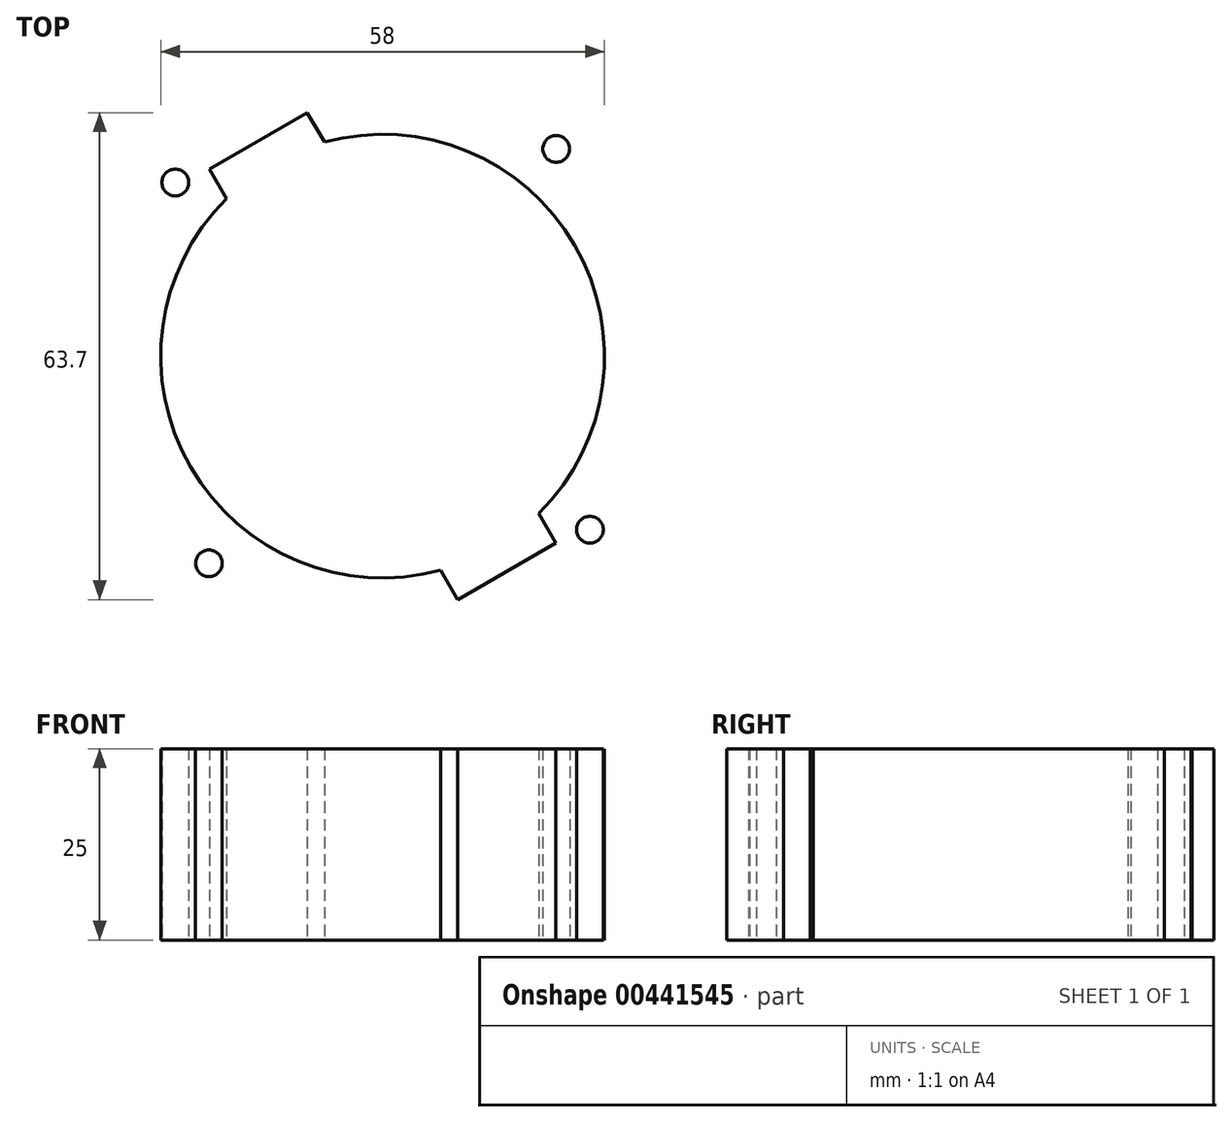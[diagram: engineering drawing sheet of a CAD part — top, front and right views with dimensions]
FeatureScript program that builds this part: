
annotation { "Feature Type Name" : "Feature", "Feature Type Description" : "" }
export const myFeature = defineFeature(function(context is Context, id is Id, definition is map)
    precondition{}
    {
        {
            var Q0;
            Q0=qCreatedBy(makeId("Top.planeOp"),FACE);
            var sketch = newSketch(context, id + "F0", { "sketchPlane" : qUnion([Q0])});
            skCircle(sketch, "E0", {"center": v(0, 0) * mm, "radius": 29 * mm});
            skLineSegment(sketch, "E1.bottom", {"start": v(-9.84, 31.85) * mm, "end": v(-22.66, 24.45) * mm});
            skLineSegment(sketch, "E1.top", {"start": v(22.66, -24.45) * mm, "end": v(9.84, -31.85) * mm});
            skLineSegment(sketch, "E1.left", {"start": v(-9.84, 31.85) * mm, "end": v(22.66, -24.45) * mm});
            skLineSegment(sketch, "E1.right", {"start": v(-22.66, 24.45) * mm, "end": v(9.84, -31.85) * mm});
            skCircle(sketch, "E2", {"center": v(22.7, 27.1) * mm, "radius": 1.75 * mm});
            skCircle(sketch, "E3", {"center": v(27.1, -22.7) * mm, "radius": 1.75 * mm});
            skCircle(sketch, "E4", {"center": v(-27.1, 22.7) * mm, "radius": 1.75 * mm});
            skCircle(sketch, "E5", {"center": v(-22.7, -27.1) * mm, "radius": 1.75 * mm});
            skSolve(sketch);
        }
        {
            var Q0;
            {var subQ0=sQuery(id+"F0.wireOp",EDGE,"E1.right");var subQ1=sQuery(id+"F0.wireOp",EDGE,"E0");var subQ2=makeQuery(id+"F0.imprint","INTERSECT",VERTEX,{"disambiguationData":[OD(0.0)],"derivedFrom":[subQ1,subQ0]});Q0=makeQuery(id+"F0.imprint","IMPRINT",FACE,{"disambiguationData":[TD([[makeQuery(id+"F0.imprint","IMPRINT",EDGE,{"disambiguationData":[TD([[subQ2,1.0]])],"derivedFrom":subQ1}),1.0]])]});}
            var Q1;
            {var subQ0=sQuery(id+"F0.wireOp",EDGE,"E1.left");var subQ1=sQuery(id+"F0.wireOp",EDGE,"E0");var subQ2=makeQuery(id+"F0.imprint","INTERSECT",VERTEX,{"disambiguationData":[OD(0.0)],"derivedFrom":[subQ1,subQ0]});Q1=makeQuery(id+"F0.imprint","IMPRINT",FACE,{"disambiguationData":[TD([[makeQuery(id+"F0.imprint","IMPRINT",EDGE,{"disambiguationData":[TD([[subQ2,1.0]])],"derivedFrom":subQ1}),1.0]])]});}
            var Q2;
            {var subQ5=sQuery(id+"F0.wireOp",EDGE,"E1.top");Q2=makeQuery(id+"F0.imprint","IMPRINT",FACE,{"disambiguationData":[TD([[makeQuery(id+"F0.imprint","IMPRINT",EDGE,{"derivedFrom":subQ5}),-1.0]])]});}
            var Q3;
            {var subQ5=sQuery(id+"F0.wireOp",EDGE,"E1.bottom");Q3=makeQuery(id+"F0.imprint","IMPRINT",FACE,{"disambiguationData":[TD([[makeQuery(id+"F0.imprint","IMPRINT",EDGE,{"derivedFrom":subQ5}),1.0]])]});}
            var Q4;
            {var subQ0=sQuery(id+"F0.wireOp",EDGE,"E1.right");var subQ1=sQuery(id+"F0.wireOp",EDGE,"E0");var subQ2=makeQuery(id+"F0.imprint","INTERSECT",VERTEX,{"disambiguationData":[OD(0.0)],"derivedFrom":[subQ1,subQ0]});Q4=makeQuery(id+"F0.imprint","IMPRINT",FACE,{"disambiguationData":[TD([[makeQuery(id+"F0.imprint","IMPRINT",EDGE,{"disambiguationData":[TD([[subQ2,-1.0]])],"derivedFrom":subQ1}),1.0]])]});}
            var Q5;
            Q5=makeQuery(id+"F0.imprint","IMPRINT",FACE,{"disambiguationData":[TD([[makeQuery(id+"F0.imprint","IMPRINT",EDGE,{"derivedFrom":sQuery(id+"F0.wireOp",EDGE,"E3")}),1.0]])]});
            var Q6;
            Q6=makeQuery(id+"F0.imprint","IMPRINT",FACE,{"disambiguationData":[TD([[makeQuery(id+"F0.imprint","IMPRINT",EDGE,{"derivedFrom":sQuery(id+"F0.wireOp",EDGE,"E2")}),1.0]])]});
            var Q7;
            Q7=makeQuery(id+"F0.imprint","IMPRINT",FACE,{"disambiguationData":[TD([[makeQuery(id+"F0.imprint","IMPRINT",EDGE,{"derivedFrom":sQuery(id+"F0.wireOp",EDGE,"E4")}),1.0]])]});
            var Q8;
            Q8=makeQuery(id+"F0.imprint","IMPRINT",FACE,{"disambiguationData":[TD([[makeQuery(id+"F0.imprint","IMPRINT",EDGE,{"derivedFrom":sQuery(id+"F0.wireOp",EDGE,"E5")}),1.0]])]});
            extrude(context, id + "F1", {"entities" : qUnion([Q0, Q1, Q2, Q3, Q4, Q5, Q6, Q7, Q8]), "endBound" : BoundingType.SYMMETRIC, "depth" : 25 * mm});
        }
    });
